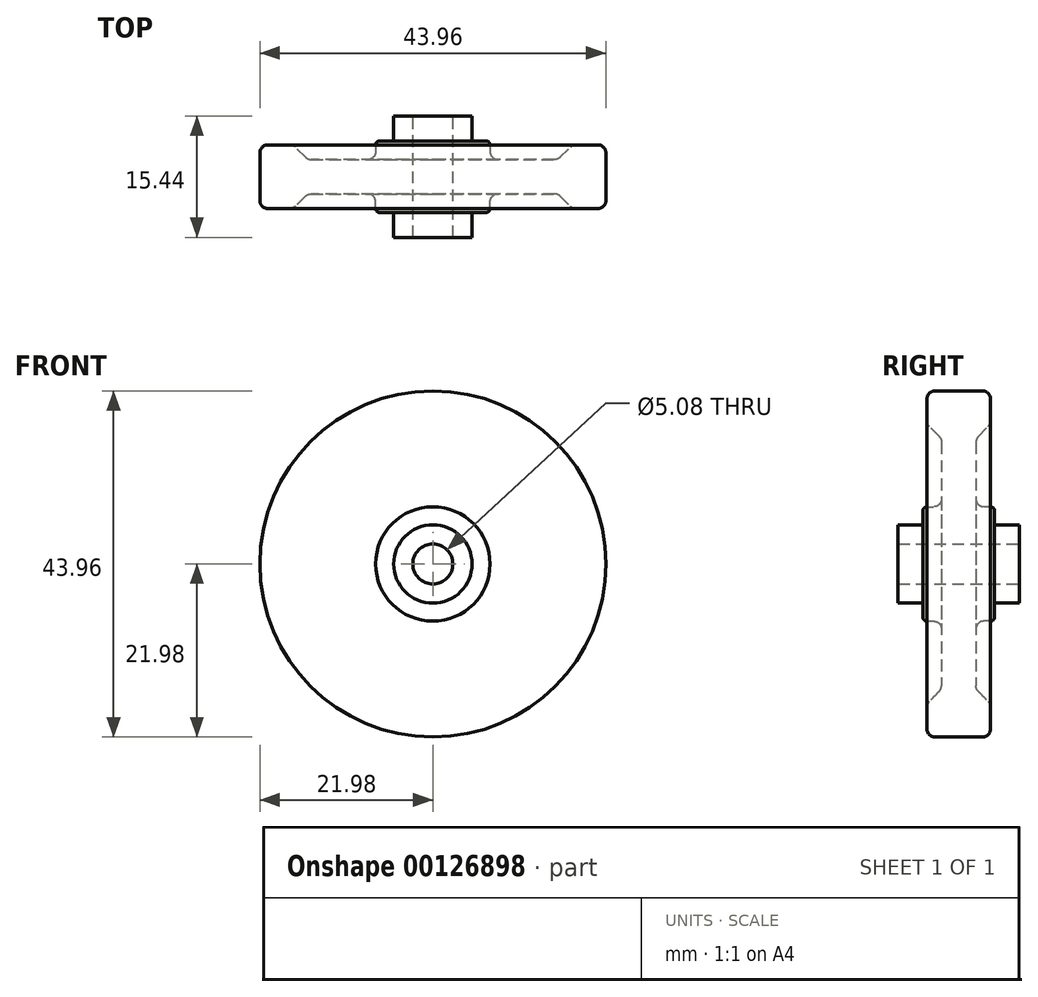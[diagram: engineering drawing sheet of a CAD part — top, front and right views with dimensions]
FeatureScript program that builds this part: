
annotation { "Feature Type Name" : "Feature", "Feature Type Description" : "" }
export const myFeature = defineFeature(function(context is Context, id is Id, definition is map)
    precondition{}
    {
        {
            var Q0;
            Q0=qCreatedBy(makeId("Right.planeOp"),FACE);
            var sketch = newSketch(context, id + "F0", { "sketchPlane" : qUnion([Q0])});
            skLineSegment(sketch, "E0", {"start": v(0, 0) * mm, "end": v(-7.72, 0) * mm, "construction": true});
            skLineSegment(sketch, "E1", {"start": v(-7.72, 2.54) * mm, "end": v(-7.72, 4.98) * mm});
            skLineSegment(sketch, "E2", {"start": v(-7.72, 4.98) * mm, "end": v(-4.55, 4.98) * mm});
            skLineSegment(sketch, "E3", {"start": v(-4.55, 4.98) * mm, "end": v(-4.55, 7.26) * mm});
            skLineSegment(sketch, "E4", {"start": v(-4.55, 7.26) * mm, "end": v(-2.18, 7.26) * mm});
            skLineSegment(sketch, "E5", {"start": v(-2.18, 7.26) * mm, "end": v(-2.18, 15.88) * mm});
            skLineSegment(sketch, "E6", {"start": v(-2.18, 15.88) * mm, "end": v(-4.04, 17.78) * mm});
            skLineSegment(sketch, "E7", {"start": v(-4.04, 17.78) * mm, "end": v(-4.04, 21.98) * mm});
            skLineSegment(sketch, "E8", {"start": v(-4.04, 21.98) * mm, "end": v(0, 21.98) * mm});
            skLineSegment(sketch, "E9", {"start": v(-7.72, 2.54) * mm, "end": v(0, 2.54) * mm});
            skLineSegment(sketch, "E10", {"start": v(0, 21.98) * mm, "end": v(0, 2.54) * mm});
            skSolve(sketch);
        }
        {
            var Q0;
            Q0=makeQuery(id+"F0.imprint","IMPRINT",FACE,{"disambiguationData":[TD([[makeQuery(id+"F0.imprint","IMPRINT",EDGE,{"derivedFrom":sQuery(id+"F0.wireOp",EDGE,"E1")}),-1.0]])]});
            var Q1;
            Q1=sQuery(id+"F0.wireOp",EDGE,"E0");
            revolve(context, id + "F1", {"entities" : qUnion([Q0]), "axis" : qUnion([Q1]), "revolveType" : RevolveType.FULL});
        }
        {
            var Q0;
            Q0=makeQuery(id+"F1.opRevolve","SWEPT_EDGE",EDGE,{"disambiguationData":[OSD([sQuery(id+"F0.wireOp",EDGE,"E4"),sQuery(id+"F0.wireOp",EDGE,"E5")])]});
            var Q1;
            Q1=makeQuery(id+"F1.opRevolve","SWEPT_EDGE",EDGE,{"disambiguationData":[OSD([sQuery(id+"F0.wireOp",EDGE,"E5"),sQuery(id+"F0.wireOp",EDGE,"E6")])]});
            var Q2;
            Q2=makeQuery(id+"F1.opRevolve","SWEPT_EDGE",EDGE,{"disambiguationData":[OSD([sQuery(id+"F0.wireOp",EDGE,"E6"),sQuery(id+"F0.wireOp",EDGE,"E7")])]});
            var Q3;
            Q3=makeQuery(id+"F1.opRevolve","SWEPT_EDGE",EDGE,{"disambiguationData":[OSD([sQuery(id+"F0.wireOp",EDGE,"E7"),sQuery(id+"F0.wireOp",EDGE,"E8")])]});
            fillet(context, id + "F2", {"entities" : qUnion([Q0, Q1, Q2, Q3]), "radius" : 1.02 * mm, "tangentPropagation" : true, "allowEdgeOverflow" : false});
        }
        {
            var Q0;
            Q0=makeQuery(id+"F1.opRevolve","SWEPT_EDGE",EDGE,{"disambiguationData":[OSD([sQuery(id+"F0.wireOp",EDGE,"E3"),sQuery(id+"F0.wireOp",EDGE,"E4")])]});
            fillet(context, id + "F3", {"entities" : qUnion([Q0]), "radius" : 0.5 * mm, "tangentPropagation" : true, "allowEdgeOverflow" : false});
        }
        {
            var Q0;
            Q0=makeQuery(id+"F1.opRevolve","SWEPT_BODY",BODY,{"disambiguationData":[OSD([sQuery(id+"F0.wireOp",EDGE,"E1"),sQuery(id+"F0.wireOp",EDGE,"E2"),sQuery(id+"F0.wireOp",EDGE,"E3"),sQuery(id+"F0.wireOp",EDGE,"E4"),sQuery(id+"F0.wireOp",EDGE,"E5"),sQuery(id+"F0.wireOp",EDGE,"E6"),sQuery(id+"F0.wireOp",EDGE,"E7"),sQuery(id+"F0.wireOp",EDGE,"E8"),sQuery(id+"F0.wireOp",EDGE,"E9"),sQuery(id+"F0.wireOp",EDGE,"E10")])]});
            var Q1;
            Q1=qCreatedBy(makeId("Front.planeOp"),FACE);
            mirror(context, id + "F4", {"operationType" : NewBodyOperationType.ADD, "entities" : qUnion([Q0]), "mirrorPlane" : qUnion([Q1])});
        }
    });
